# Revit family: Grille-Supply-Carnes-RNAM-Extruded_Aluminum
name_source: partatom
category: Duct Accessories
revit_build: Autodesk Revit MEP 2014 (Build: 20130308_1515(x64)
units: mm (PartAtom-declared; Revit-internal decimal feet)

## types (20) — shared parameters
Assembly Code = D3040100
Blade Spacing = 3/4"
Catalog = http://www.carnes.com
Default Elevation = 96"
Description = Square and Rectangular Registers and Grilles
Flow = 0 CFM
Manufacturer = CARNES COMPANY
Model = RNAM
Product Page URL = http://www.carnes.com
Return Connection = Diffuser Return Connector
Return Connector = Yes
Revit Object Download Link = http://library.smartbim.com
Specification Sheet = http://www.carnes.com
Subcatagory = Air Distribution
URL = http://www.carnes.com
Unit = Metal - Carnes - Extruded-Aluminum

## per-type parameters (varying)
| type | Height | Inner Depth | Inner Width | Width |
| RNAM 10 x 6 | 6" | 3 1/2" | 7 1/2" | 10" |
| RNAM 12 x 6 | 6" | 3 1/2" | 9 1/2" | 12" |
| RNAM 10 x 8 | 8" | 5 1/2" | 7 1/2" | 10" |
| RNAM 12 x 8 | 8" | 5 1/2" | 9 1/2" | 12" |
| RNAM 18 x 6 | 6" | 3 1/2" | 15 1/2" | 18" |
| RNAM 12 x 12 | 12" | 9 1/2" | 9 1/2" | 12" |
| RNAM 18 x 12 | 12" | 9 1/2" | 15 1/2" | 18" |
| RNAM 24 x 12 | 12" | 9 1/2" | 21 1/2" | 24" |
| RNAM 18 x 18 | 18" | 15 1/2" | 15 1/2" | 18" |
| RNAM 30 x 12 | 12" | 9 1/2" | 27 1/2" | 30" |
| RNAM 24 x 18 | 18" | 15 1/2" | 21 1/2" | 24" |
| RNAM 30 x 18 | 18" | 15 1/2" | 27 1/2" | 30" |
| RNAM 24 x 24 | 24" | 21 1/2" | 21 1/2" | 24" |
| RNAM 36 x 18 | 18" | 15 1/2" | 33 1/2" | 36" |
| RNAM 30 x 24 | 24" | 21 1/2" | 27 1/2" | 30" |
| RNAM 36 x 24 | 24" | 21 1/2" | 33 1/2" | 36" |
| RNAM 36 x 30 | 30" | 27 1/2" | 33 1/2" | 36" |
| RNAM 48 x 24 | 24" | 21 1/2" | 45 1/2" | 48" |
| RNAM 48 x 30 | 30" | 27 1/2" | 45 1/2" | 48" |
| RNAM 48 x 36 | 36" | 33 1/2" | 45 1/2" | 48" |

## geometry (parser evidence)
native form markers: Blend x4, Sweep x3
no freeform markers — native parametric forms only
